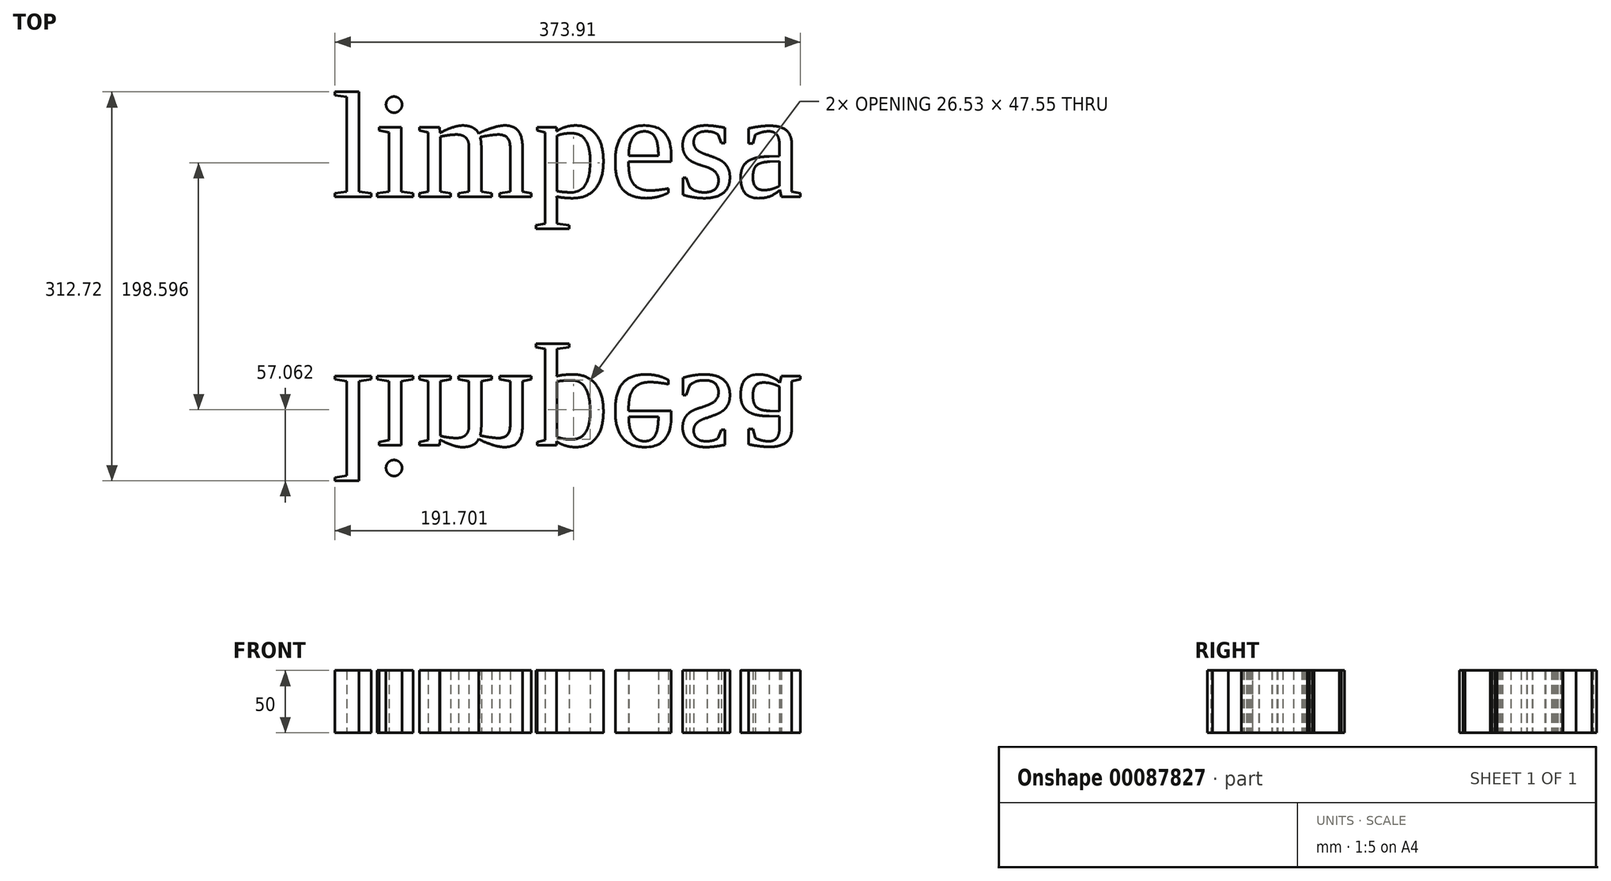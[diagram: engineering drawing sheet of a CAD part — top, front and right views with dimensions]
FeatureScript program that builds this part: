
annotation { "Feature Type Name" : "Feature", "Feature Type Description" : "" }
export const myFeature = defineFeature(function(context is Context, id is Id, definition is map)
    precondition{}
    {
        {
            var Q0;
            Q0=qCreatedBy(makeId("Top.planeOp"),FACE);
            var sketch = newSketch(context, id + "F0", { "sketchPlane" : qUnion([Q0])});
            skText(sketch, "E0", { "text": "limpesa\n", "fontName": "Tinos-Regular.ttf"});
            const initialGuessF0  = {"E0": [-0.1923, 0.07203, 1, 0, 0.0875]};
            skSetInitialGuess(sketch, initialGuessF0);
            skSolve(sketch);
        }
        {
            var Q0;
            Q0 = qSketchRegion(id + "F0", true);
            extrude(context, id + "F1", {"entities" : qUnion([Q0]), "endBound" : BoundingType.SYMMETRIC, "depth" : 50 * mm});
        }
        {
            var Q0;
            Q0=makeQuery(id+"F1.opExtrude","SWEPT_BODY",BODY,{"disambiguationData":[OSD([sQuery(id+"F0.wireOp",EDGE,"E0.sketch_text.stroke-69"),sQuery(id+"F0.wireOp",EDGE,"E0.sketch_text.stroke-70"),sQuery(id+"F0.wireOp",EDGE,"E0.sketch_text.stroke-71"),sQuery(id+"F0.wireOp",EDGE,"E0.sketch_text.stroke-72"),sQuery(id+"F0.wireOp",EDGE,"E0.sketch_text.stroke-73"),sQuery(id+"F0.wireOp",EDGE,"E0.sketch_text.stroke-74"),sQuery(id+"F0.wireOp",EDGE,"E0.sketch_text.stroke-75"),sQuery(id+"F0.wireOp",EDGE,"E0.sketch_text.stroke-76"),sQuery(id+"F0.wireOp",EDGE,"E0.sketch_text.stroke-77"),sQuery(id+"F0.wireOp",EDGE,"E0.sketch_text.stroke-78"),sQuery(id+"F0.wireOp",EDGE,"E0.sketch_text.stroke-79"),sQuery(id+"F0.wireOp",EDGE,"E0.sketch_text.stroke-80"),sQuery(id+"F0.wireOp",EDGE,"E0.sketch_text.stroke-81"),sQuery(id+"F0.wireOp",EDGE,"E0.sketch_text.stroke-82"),sQuery(id+"F0.wireOp",EDGE,"E0.sketch_text.stroke-83"),sQuery(id+"F0.wireOp",EDGE,"E0.sketch_text.stroke-84"),sQuery(id+"F0.wireOp",EDGE,"E0.sketch_text.stroke-85"),sQuery(id+"F0.wireOp",EDGE,"E0.sketch_text.stroke-86"),sQuery(id+"F0.wireOp",EDGE,"E0.sketch_text.stroke-87")])]});
            var Q1;
            Q1=makeQuery(id+"F1.opExtrude","SWEPT_BODY",BODY,{"disambiguationData":[OSD([sQuery(id+"F0.wireOp",EDGE,"E0.sketch_text.stroke-16"),sQuery(id+"F0.wireOp",EDGE,"E0.sketch_text.stroke-17"),sQuery(id+"F0.wireOp",EDGE,"E0.sketch_text.stroke-18"),sQuery(id+"F0.wireOp",EDGE,"E0.sketch_text.stroke-19"),sQuery(id+"F0.wireOp",EDGE,"E0.sketch_text.stroke-20"),sQuery(id+"F0.wireOp",EDGE,"E0.sketch_text.stroke-21"),sQuery(id+"F0.wireOp",EDGE,"E0.sketch_text.stroke-22"),sQuery(id+"F0.wireOp",EDGE,"E0.sketch_text.stroke-23"),sQuery(id+"F0.wireOp",EDGE,"E0.sketch_text.stroke-24"),sQuery(id+"F0.wireOp",EDGE,"E0.sketch_text.stroke-25"),sQuery(id+"F0.wireOp",EDGE,"E0.sketch_text.stroke-26"),sQuery(id+"F0.wireOp",EDGE,"E0.sketch_text.stroke-27"),sQuery(id+"F0.wireOp",EDGE,"E0.sketch_text.stroke-28"),sQuery(id+"F0.wireOp",EDGE,"E0.sketch_text.stroke-29"),sQuery(id+"F0.wireOp",EDGE,"E0.sketch_text.stroke-30"),sQuery(id+"F0.wireOp",EDGE,"E0.sketch_text.stroke-31"),sQuery(id+"F0.wireOp",EDGE,"E0.sketch_text.stroke-32"),sQuery(id+"F0.wireOp",EDGE,"E0.sketch_text.stroke-33"),sQuery(id+"F0.wireOp",EDGE,"E0.sketch_text.stroke-34"),sQuery(id+"F0.wireOp",EDGE,"E0.sketch_text.stroke-35"),sQuery(id+"F0.wireOp",EDGE,"E0.sketch_text.stroke-36"),sQuery(id+"F0.wireOp",EDGE,"E0.sketch_text.stroke-37"),sQuery(id+"F0.wireOp",EDGE,"E0.sketch_text.stroke-38"),sQuery(id+"F0.wireOp",EDGE,"E0.sketch_text.stroke-39"),sQuery(id+"F0.wireOp",EDGE,"E0.sketch_text.stroke-40"),sQuery(id+"F0.wireOp",EDGE,"E0.sketch_text.stroke-41"),sQuery(id+"F0.wireOp",EDGE,"E0.sketch_text.stroke-42"),sQuery(id+"F0.wireOp",EDGE,"E0.sketch_text.stroke-43")])]});
            var Q2;
            Q2=makeQuery(id+"F1.opExtrude","SWEPT_BODY",BODY,{"disambiguationData":[OSD([sQuery(id+"F0.wireOp",EDGE,"E0.sketch_text.stroke-8"),sQuery(id+"F0.wireOp",EDGE,"E0.sketch_text.stroke-9"),sQuery(id+"F0.wireOp",EDGE,"E0.sketch_text.stroke-10"),sQuery(id+"F0.wireOp",EDGE,"E0.sketch_text.stroke-11"),sQuery(id+"F0.wireOp",EDGE,"E0.sketch_text.stroke-12"),sQuery(id+"F0.wireOp",EDGE,"E0.sketch_text.stroke-13"),sQuery(id+"F0.wireOp",EDGE,"E0.sketch_text.stroke-14"),sQuery(id+"F0.wireOp",EDGE,"E0.sketch_text.stroke-15")])]});
            var Q3;
            Q3=makeQuery(id+"F1.opExtrude","SWEPT_BODY",BODY,{"disambiguationData":[OSD([sQuery(id+"F0.wireOp",EDGE,"E0.sketch_text.stroke-44"),sQuery(id+"F0.wireOp",EDGE,"E0.sketch_text.stroke-45"),sQuery(id+"F0.wireOp",EDGE,"E0.sketch_text.stroke-46"),sQuery(id+"F0.wireOp",EDGE,"E0.sketch_text.stroke-47"),sQuery(id+"F0.wireOp",EDGE,"E0.sketch_text.stroke-48"),sQuery(id+"F0.wireOp",EDGE,"E0.sketch_text.stroke-49"),sQuery(id+"F0.wireOp",EDGE,"E0.sketch_text.stroke-50"),sQuery(id+"F0.wireOp",EDGE,"E0.sketch_text.stroke-51"),sQuery(id+"F0.wireOp",EDGE,"E0.sketch_text.stroke-52"),sQuery(id+"F0.wireOp",EDGE,"E0.sketch_text.stroke-53"),sQuery(id+"F0.wireOp",EDGE,"E0.sketch_text.stroke-54"),sQuery(id+"F0.wireOp",EDGE,"E0.sketch_text.stroke-55"),sQuery(id+"F0.wireOp",EDGE,"E0.sketch_text.stroke-56"),sQuery(id+"F0.wireOp",EDGE,"E0.sketch_text.stroke-57"),sQuery(id+"F0.wireOp",EDGE,"E0.sketch_text.stroke-58"),sQuery(id+"F0.wireOp",EDGE,"E0.sketch_text.stroke-59"),sQuery(id+"F0.wireOp",EDGE,"E0.sketch_text.stroke-60"),sQuery(id+"F0.wireOp",EDGE,"E0.sketch_text.stroke-61"),sQuery(id+"F0.wireOp",EDGE,"E0.sketch_text.stroke-62"),sQuery(id+"F0.wireOp",EDGE,"E0.sketch_text.stroke-63"),sQuery(id+"F0.wireOp",EDGE,"E0.sketch_text.stroke-64"),sQuery(id+"F0.wireOp",EDGE,"E0.sketch_text.stroke-65"),sQuery(id+"F0.wireOp",EDGE,"E0.sketch_text.stroke-66"),sQuery(id+"F0.wireOp",EDGE,"E0.sketch_text.stroke-67"),sQuery(id+"F0.wireOp",EDGE,"E0.sketch_text.stroke-68")])]});
            var Q4;
            Q4=makeQuery(id+"F1.opExtrude","SWEPT_BODY",BODY,{"disambiguationData":[OSD([sQuery(id+"F0.wireOp",EDGE,"E0.sketch_text.stroke-4"),sQuery(id+"F0.wireOp",EDGE,"E0.sketch_text.stroke-5"),sQuery(id+"F0.wireOp",EDGE,"E0.sketch_text.stroke-6"),sQuery(id+"F0.wireOp",EDGE,"E0.sketch_text.stroke-7")])]});
            var Q5;
            Q5=makeQuery(id+"F1.opExtrude","SWEPT_BODY",BODY,{"disambiguationData":[OSD([sQuery(id+"F0.wireOp",EDGE,"E0.sketch_text.stroke-0"),sQuery(id+"F0.wireOp",EDGE,"E0.sketch_text.stroke-1"),sQuery(id+"F0.wireOp",EDGE,"E0.sketch_text.stroke-2"),sQuery(id+"F0.wireOp",EDGE,"E0.sketch_text.stroke-3")])]});
            var Q6;
            Q6=makeQuery(id+"F1.opExtrude","SWEPT_BODY",BODY,{"disambiguationData":[OSD([sQuery(id+"F0.wireOp",EDGE,"E0.sketch_text.stroke-88"),sQuery(id+"F0.wireOp",EDGE,"E0.sketch_text.stroke-89"),sQuery(id+"F0.wireOp",EDGE,"E0.sketch_text.stroke-90"),sQuery(id+"F0.wireOp",EDGE,"E0.sketch_text.stroke-91"),sQuery(id+"F0.wireOp",EDGE,"E0.sketch_text.stroke-92"),sQuery(id+"F0.wireOp",EDGE,"E0.sketch_text.stroke-93"),sQuery(id+"F0.wireOp",EDGE,"E0.sketch_text.stroke-94"),sQuery(id+"F0.wireOp",EDGE,"E0.sketch_text.stroke-95"),sQuery(id+"F0.wireOp",EDGE,"E0.sketch_text.stroke-96"),sQuery(id+"F0.wireOp",EDGE,"E0.sketch_text.stroke-97"),sQuery(id+"F0.wireOp",EDGE,"E0.sketch_text.stroke-98"),sQuery(id+"F0.wireOp",EDGE,"E0.sketch_text.stroke-99"),sQuery(id+"F0.wireOp",EDGE,"E0.sketch_text.stroke-100"),sQuery(id+"F0.wireOp",EDGE,"E0.sketch_text.stroke-101"),sQuery(id+"F0.wireOp",EDGE,"E0.sketch_text.stroke-102"),sQuery(id+"F0.wireOp",EDGE,"E0.sketch_text.stroke-103"),sQuery(id+"F0.wireOp",EDGE,"E0.sketch_text.stroke-104"),sQuery(id+"F0.wireOp",EDGE,"E0.sketch_text.stroke-105"),sQuery(id+"F0.wireOp",EDGE,"E0.sketch_text.stroke-106"),sQuery(id+"F0.wireOp",EDGE,"E0.sketch_text.stroke-107"),sQuery(id+"F0.wireOp",EDGE,"E0.sketch_text.stroke-108"),sQuery(id+"F0.wireOp",EDGE,"E0.sketch_text.stroke-109"),sQuery(id+"F0.wireOp",EDGE,"E0.sketch_text.stroke-110"),sQuery(id+"F0.wireOp",EDGE,"E0.sketch_text.stroke-111"),sQuery(id+"F0.wireOp",EDGE,"E0.sketch_text.stroke-112")])]});
            var Q7;
            Q7=makeQuery(id+"F1.opExtrude","SWEPT_BODY",BODY,{"disambiguationData":[OSD([sQuery(id+"F0.wireOp",EDGE,"E0.sketch_text.stroke-113"),sQuery(id+"F0.wireOp",EDGE,"E0.sketch_text.stroke-114"),sQuery(id+"F0.wireOp",EDGE,"E0.sketch_text.stroke-115"),sQuery(id+"F0.wireOp",EDGE,"E0.sketch_text.stroke-116"),sQuery(id+"F0.wireOp",EDGE,"E0.sketch_text.stroke-117"),sQuery(id+"F0.wireOp",EDGE,"E0.sketch_text.stroke-118"),sQuery(id+"F0.wireOp",EDGE,"E0.sketch_text.stroke-119"),sQuery(id+"F0.wireOp",EDGE,"E0.sketch_text.stroke-120"),sQuery(id+"F0.wireOp",EDGE,"E0.sketch_text.stroke-121"),sQuery(id+"F0.wireOp",EDGE,"E0.sketch_text.stroke-122"),sQuery(id+"F0.wireOp",EDGE,"E0.sketch_text.stroke-123"),sQuery(id+"F0.wireOp",EDGE,"E0.sketch_text.stroke-124"),sQuery(id+"F0.wireOp",EDGE,"E0.sketch_text.stroke-125"),sQuery(id+"F0.wireOp",EDGE,"E0.sketch_text.stroke-126"),sQuery(id+"F0.wireOp",EDGE,"E0.sketch_text.stroke-127"),sQuery(id+"F0.wireOp",EDGE,"E0.sketch_text.stroke-128"),sQuery(id+"F0.wireOp",EDGE,"E0.sketch_text.stroke-129"),sQuery(id+"F0.wireOp",EDGE,"E0.sketch_text.stroke-130"),sQuery(id+"F0.wireOp",EDGE,"E0.sketch_text.stroke-131"),sQuery(id+"F0.wireOp",EDGE,"E0.sketch_text.stroke-132"),sQuery(id+"F0.wireOp",EDGE,"E0.sketch_text.stroke-133"),sQuery(id+"F0.wireOp",EDGE,"E0.sketch_text.stroke-134"),sQuery(id+"F0.wireOp",EDGE,"E0.sketch_text.stroke-135"),sQuery(id+"F0.wireOp",EDGE,"E0.sketch_text.stroke-136"),sQuery(id+"F0.wireOp",EDGE,"E0.sketch_text.stroke-137"),sQuery(id+"F0.wireOp",EDGE,"E0.sketch_text.stroke-138"),sQuery(id+"F0.wireOp",EDGE,"E0.sketch_text.stroke-139")])]});
            var Q8;
            Q8=makeQuery(id+"F1.opExtrude","SWEPT_BODY",BODY,{"disambiguationData":[OSD([sQuery(id+"F0.wireOp",EDGE,"E0.sketch_text.stroke-144"),sQuery(id+"F0.wireOp",EDGE,"E0.sketch_text.stroke-145"),sQuery(id+"F0.wireOp",EDGE,"E0.sketch_text.stroke-146"),sQuery(id+"F0.wireOp",EDGE,"E0.sketch_text.stroke-147"),sQuery(id+"F0.wireOp",EDGE,"E0.sketch_text.stroke-148"),sQuery(id+"F0.wireOp",EDGE,"E0.sketch_text.stroke-149"),sQuery(id+"F0.wireOp",EDGE,"E0.sketch_text.stroke-150"),sQuery(id+"F0.wireOp",EDGE,"E0.sketch_text.stroke-151"),sQuery(id+"F0.wireOp",EDGE,"E0.sketch_text.stroke-152"),sQuery(id+"F0.wireOp",EDGE,"E0.sketch_text.stroke-153"),sQuery(id+"F0.wireOp",EDGE,"E0.sketch_text.stroke-154"),sQuery(id+"F0.wireOp",EDGE,"E0.sketch_text.stroke-155"),sQuery(id+"F0.wireOp",EDGE,"E0.sketch_text.stroke-156"),sQuery(id+"F0.wireOp",EDGE,"E0.sketch_text.stroke-157"),sQuery(id+"F0.wireOp",EDGE,"E0.sketch_text.stroke-158"),sQuery(id+"F0.wireOp",EDGE,"E0.sketch_text.stroke-159"),sQuery(id+"F0.wireOp",EDGE,"E0.sketch_text.stroke-160"),sQuery(id+"F0.wireOp",EDGE,"E0.sketch_text.stroke-161"),sQuery(id+"F0.wireOp",EDGE,"E0.sketch_text.stroke-162"),sQuery(id+"F0.wireOp",EDGE,"E0.sketch_text.stroke-163"),sQuery(id+"F0.wireOp",EDGE,"E0.sketch_text.stroke-164"),sQuery(id+"F0.wireOp",EDGE,"E0.sketch_text.stroke-165"),sQuery(id+"F0.wireOp",EDGE,"E0.sketch_text.stroke-166"),sQuery(id+"F0.wireOp",EDGE,"E0.sketch_text.stroke-167"),sQuery(id+"F0.wireOp",EDGE,"E0.sketch_text.stroke-168"),sQuery(id+"F0.wireOp",EDGE,"E0.sketch_text.stroke-169"),sQuery(id+"F0.wireOp",EDGE,"E0.sketch_text.stroke-170"),sQuery(id+"F0.wireOp",EDGE,"E0.sketch_text.stroke-171")])]});
            var Q9;
            Q9=qCreatedBy(makeId("Front.planeOp"),FACE);
            mirror(context, id + "F2", {"entities" : qUnion([Q0, Q1, Q2, Q3, Q4, Q5, Q6, Q7, Q8]), "mirrorPlane" : qUnion([Q9])});
        }
    });
